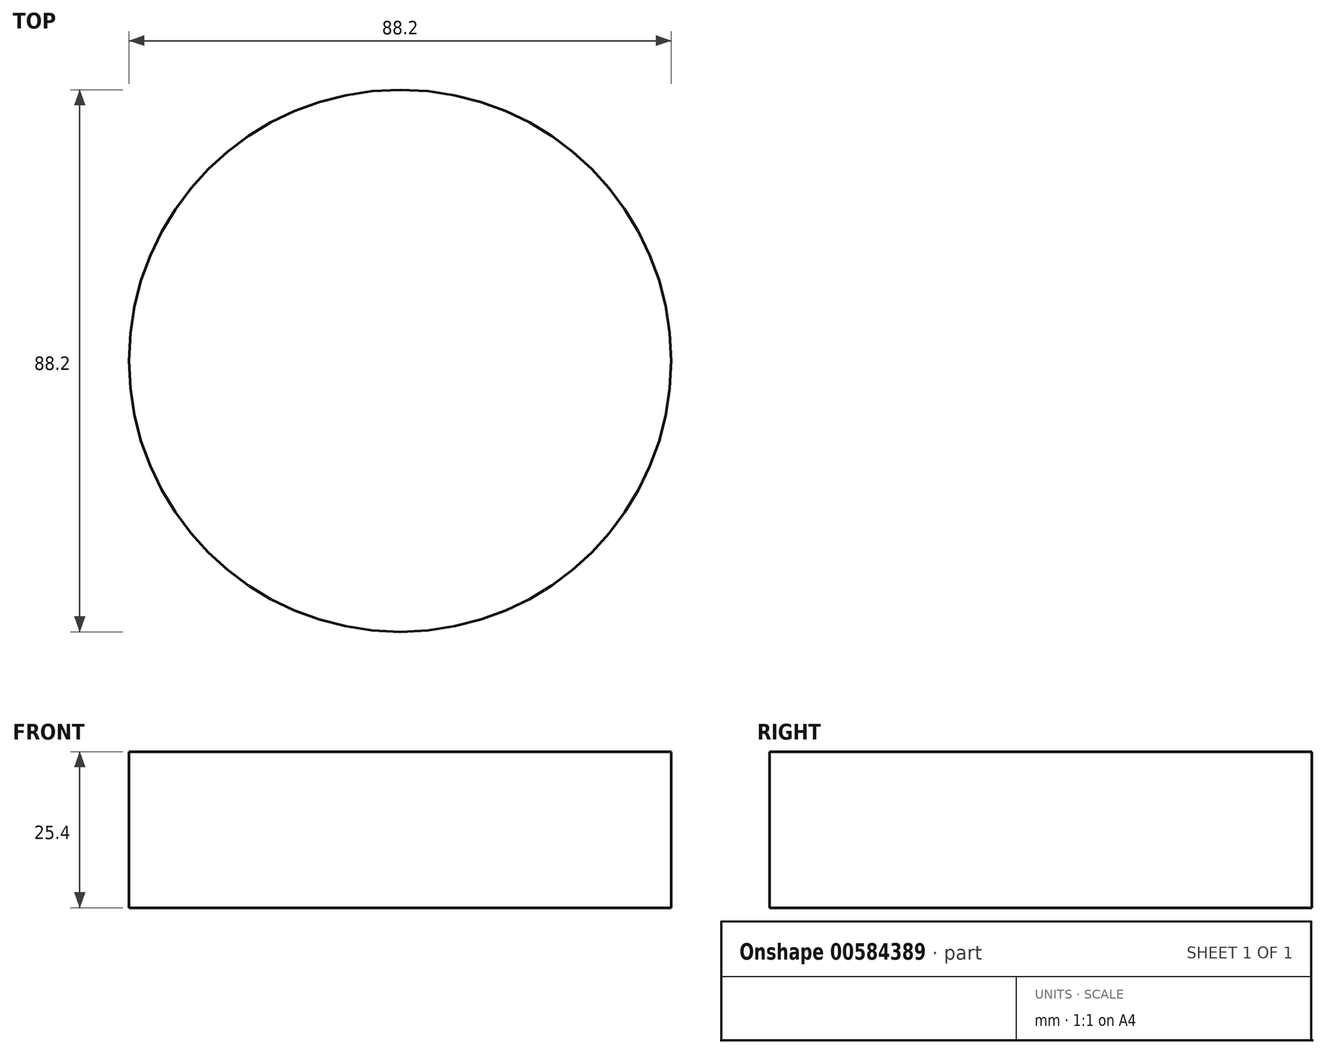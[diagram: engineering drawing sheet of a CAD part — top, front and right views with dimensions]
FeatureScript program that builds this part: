
annotation { "Feature Type Name" : "Feature", "Feature Type Description" : "" }
export const myFeature = defineFeature(function(context is Context, id is Id, definition is map)
    precondition{}
    {
        {
            var Q0;
            Q0=qCreatedBy(makeId("Top.planeOp"),FACE);
            var sketch = newSketch(context, id + "F0", { "sketchPlane" : qUnion([Q0])});
            skCircle(sketch, "E0", {"center": v(0, 0) * mm, "radius": 44.1 * mm});
            skSolve(sketch);
        }
        {
            var Q0;
            Q0=makeQuery(id+"F0.imprint","IMPRINT",FACE,{"disambiguationData":[TD([[makeQuery(id+"F0.imprint","IMPRINT",EDGE,{"derivedFrom":sQuery(id+"F0.wireOp",EDGE,"E0")}),1.0]])]});
            extrude(context, id + "F1", {"entities" : qUnion([Q0]), "depth" : 25.4 * mm, "offsetDistance" : 25.4 * mm});
        }
    });
